# Revit family: MaviGard Неадресный извещатель токсичной концентрации угарного газа
name_source: partatom
category: Fire Alarm Devices
units: mm (PartAtom-declared; Revit-internal decimal feet)

## family parameters
Cut with Voids When Loaded = No
Host = Face
Maintain Annotation Orientation = Yes
OmniClass Number = 23.85.30.21
OmniClass Title = Environmental Detection/Registration
Part Type = Normal
Room Calculation Point = No
Round Connector Dimension = Use Diameter
Shared = No

## types (1)
- Извещатель токсичной концентрации угарного газа потолочного и настенного типа
    Cost = 0 $
    Default Elevation = 0 mm  [stored 0 ft]
    Description = Неадресный извещатель угарного газа
    Manufacturer = Mavili Elektronik Ticaret A.Ş.
    Model = MaviGard
    URL = https://www.mavili.com.tr
    Адрес №1 = Şerifali Mahallesi Kutup Sokak No:27/1-2-4 Ümraniye TR-34775 İSTANBUL
    Вторичный материал = Пластмассовый
    Гарантийный срок = Года
    Гарантийный срок запчастей = 2
    Гарантия срока службы = 2
    Главный Материал = Белый пластмассовый PC/ABS
    Диапазон рабочего напряжения = 18-33В пост. ток
    Инструкция по установке = https://mavilielektronik.com
    Класс защиты = IP42
    Код продукта = TGDR-1224M
    Монтажная высота = 15-25 см ниже потолка
    Монтажная поверхность = Настенная или потолочная установка
    Номер телефона = (+)90 216 466 45 05
    Номер факса = (+)90 216 466 45 10
    Производительность кода = EN 50194-1
    Рабочая Температура = (-10°C) - (+50°C)
    Рабочее напряжение (по умолчанию) = 24 В пост. ток
    Резервное питание = 24 В пост. ток
    Совместимые базы для монтажа = MG-3500
    Цвет = Белый

note: [stored X ft] marks values corroborated as IEEE doubles in the binary element streams (Revit-internal decimal feet)

## geometry (parser evidence)
native form markers: Sweep x2
no freeform markers — native parametric forms only
